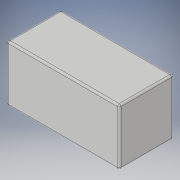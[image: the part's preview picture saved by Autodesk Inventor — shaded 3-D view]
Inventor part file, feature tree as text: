
AUTODESK INVENTOR PART (.ipt)
format: ipt  version: 2019.4 (Build 234330000, 330)  size: 103,936 bytes
history: native  units: mm
features: other x1, extrude x1, fillet x1, sketch x1
ambient origin geometry x8: Origin, YZ Plane, XZ Plane, XY Plane, X Axis, Y Axis, Z Axis, Center Point
bodies: Body1 (feature_tree)
feature tree (4):
  other  "實體1"
  extrude  "擠出1"  Depth=10.0mm
  fillet  "圓角1"  Radius=5.0mm
  sketch  "草圖1"
